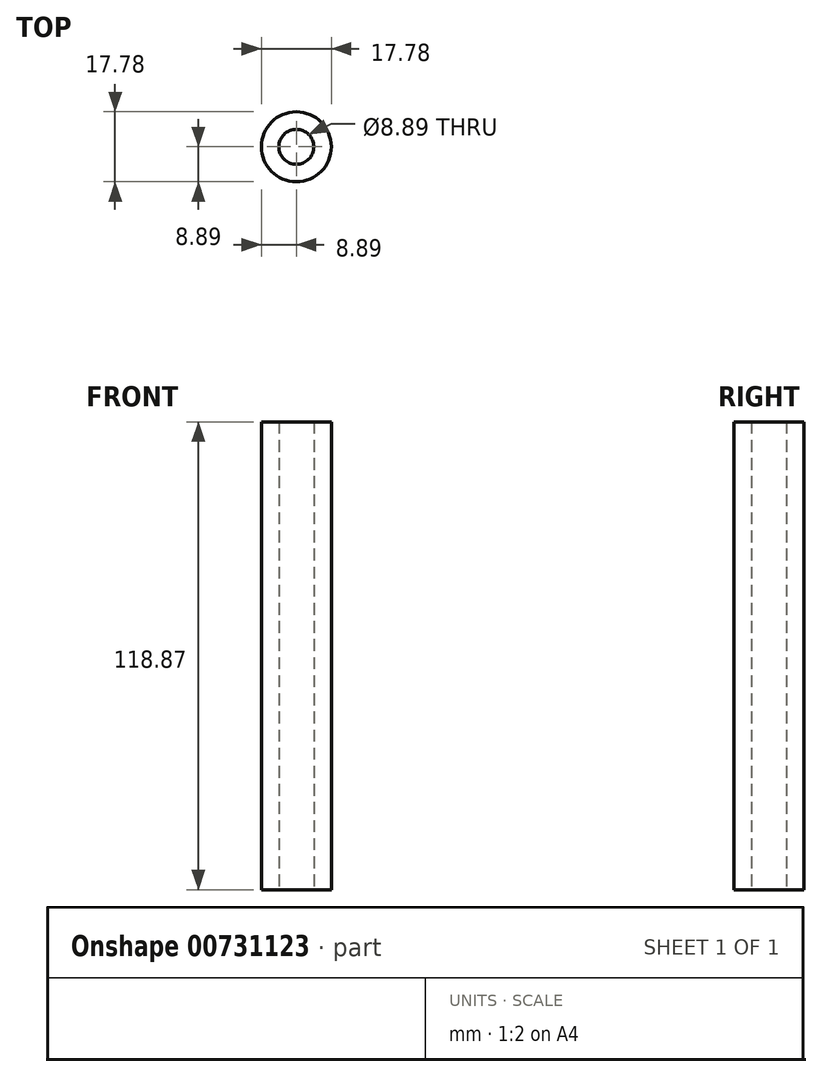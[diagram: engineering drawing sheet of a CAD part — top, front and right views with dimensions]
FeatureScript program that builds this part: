
annotation { "Feature Type Name" : "Feature", "Feature Type Description" : "" }
export const myFeature = defineFeature(function(context is Context, id is Id, definition is map)
    precondition{}
    {
        {
            var Q0;
            Q0=qCreatedBy(makeId("Top.planeOp"),FACE);
            var sketch = newSketch(context, id + "F0", { "sketchPlane" : qUnion([Q0])});
            skCircle(sketch, "E0", {"center": v(0, 0) * mm, "radius": 8.9 * mm});
            skCircle(sketch, "E1", {"center": v(0, 0) * mm, "radius": 4.45 * mm});
            skSolve(sketch);
        }
        {
            var Q0;
            Q0 = qSketchRegion(id + "F0", true);
            extrude(context, id + "F1", {"entities" : qUnion([Q0]), "depth" : 118.87 * mm, "offsetDistance" : 25.4 * mm});
        }
    });
